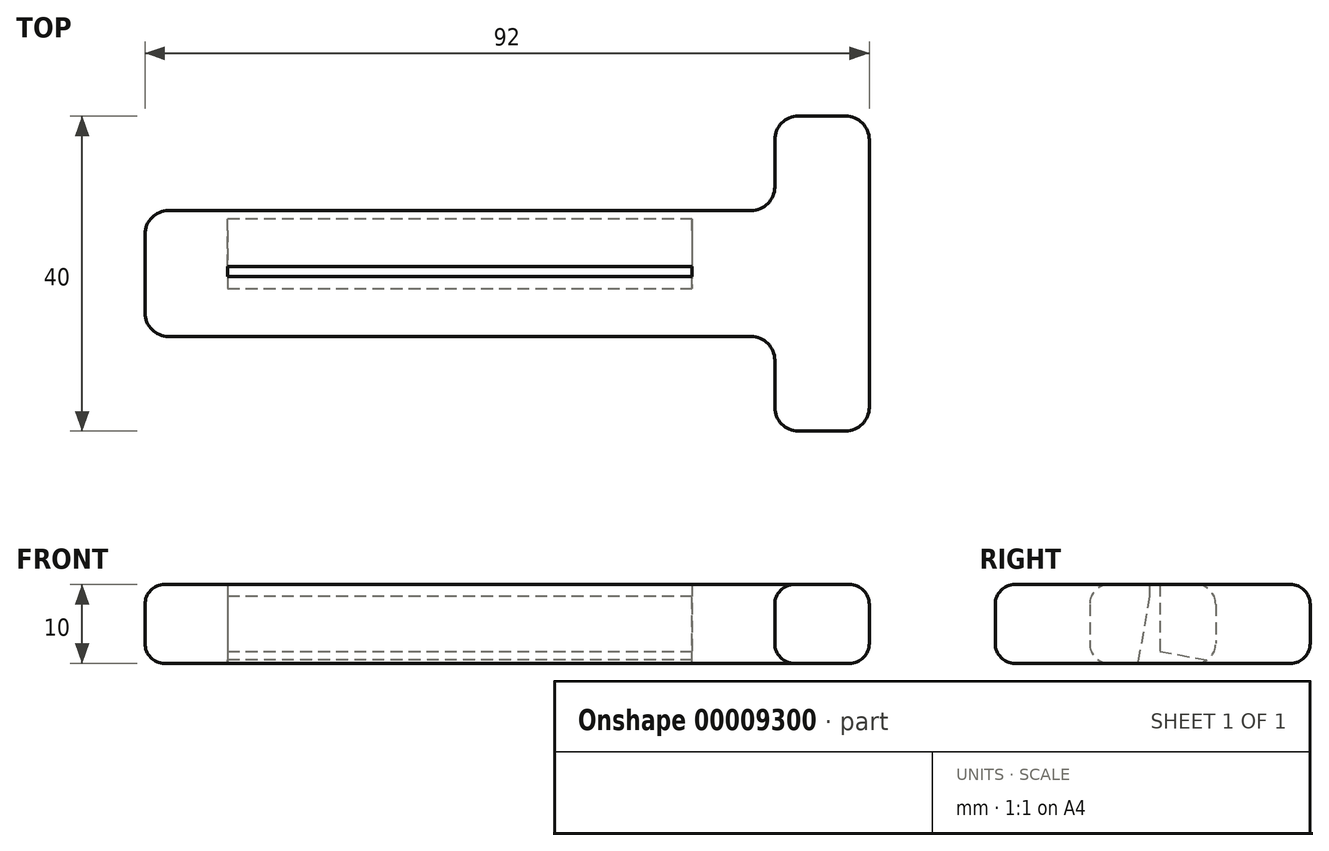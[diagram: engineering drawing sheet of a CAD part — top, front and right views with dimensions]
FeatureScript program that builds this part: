
annotation { "Feature Type Name" : "Feature", "Feature Type Description" : "" }
export const myFeature = defineFeature(function(context is Context, id is Id, definition is map)
    precondition{}
    {
        {
            var Q0;
            Q0=qCreatedBy(makeId("Top.planeOp"),FACE);
            var sketch = newSketch(context, id + "F0", { "sketchPlane" : qUnion([Q0])});
            skLineSegment(sketch, "E0.bottom", {"start": v(-31.18, 12.18) * mm, "end": v(27.82, 12.18) * mm});
            skLineSegment(sketch, "E0.top", {"start": v(-31.18, 10.88) * mm, "end": v(27.82, 10.88) * mm});
            skLineSegment(sketch, "E0.left", {"start": v(-31.18, 12.18) * mm, "end": v(-31.18, 10.88) * mm});
            skLineSegment(sketch, "E0.right", {"start": v(27.82, 12.18) * mm, "end": v(27.82, 10.88) * mm});
            skLineSegment(sketch, "E1.bottom", {"start": v(-38.68, 19.28) * mm, "end": v(35.32, 19.28) * mm});
            skLineSegment(sketch, "E1.top", {"start": v(-38.68, 3.28) * mm, "end": v(35.32, 3.28) * mm});
            skLineSegment(sketch, "E1.left", {"start": v(-41.68, 16.28) * mm, "end": v(-41.68, 6.28) * mm});
            skPoint(sketch, "E2.visualSharp", {"position": v(-41.68, 19.28) * mm});
            skArc(sketch, "E2.filletArc", {"start": v(-38.68, 19.28) * mm, "mid": v(-40.8, 18.4) * mm, "end": v(-41.68, 16.28) * mm});
            skPoint(sketch, "E3.visualSharp", {"position": v(-41.68, 3.28) * mm});
            skArc(sketch, "E3.filletArc", {"start": v(-41.68, 6.28) * mm, "mid": v(-40.8, 4.16) * mm, "end": v(-38.68, 3.28) * mm});
            skLineSegment(sketch, "E4.bottom", {"start": v(41.32, 31.28) * mm, "end": v(47.32, 31.28) * mm});
            skLineSegment(sketch, "E4.top", {"start": v(41.32, -8.72) * mm, "end": v(47.32, -8.72) * mm});
            skLineSegment(sketch, "E4.left", {"start": v(38.32, 0.28) * mm, "end": v(38.32, -5.72) * mm});
            skLineSegment(sketch, "E4.right", {"start": v(50.32, 28.28) * mm, "end": v(50.32, -5.72) * mm});
            skPoint(sketch, "E5.visualSharp", {"position": v(38.32, 31.28) * mm});
            skArc(sketch, "E5.filletArc", {"start": v(41.32, 31.28) * mm, "mid": v(39.2, 30.4) * mm, "end": v(38.32, 28.28) * mm});
            skPoint(sketch, "E6.visualSharp", {"position": v(50.32, 31.28) * mm});
            skArc(sketch, "E6.filletArc", {"start": v(50.32, 28.28) * mm, "mid": v(49.44, 30.4) * mm, "end": v(47.32, 31.28) * mm});
            skPoint(sketch, "E7.visualSharp", {"position": v(50.32, -8.72) * mm});
            skArc(sketch, "E7.filletArc", {"start": v(47.32, -8.72) * mm, "mid": v(49.44, -7.84) * mm, "end": v(50.32, -5.72) * mm});
            skPoint(sketch, "E8.visualSharp", {"position": v(38.32, -8.72) * mm});
            skArc(sketch, "E8.filletArc", {"start": v(38.32, -5.72) * mm, "mid": v(39.2, -7.84) * mm, "end": v(41.32, -8.72) * mm});
            skPoint(sketch, "E9.newPointA", {"position": v(39.32, 3.28) * mm});
            skArc(sketch, "E9.filletArc", {"start": v(38.32, 0.28) * mm, "mid": v(37.44, 2.4) * mm, "end": v(35.32, 3.28) * mm});
            skLineSegment(sketch, "E10", {"start": v(38.32, 28.28) * mm, "end": v(38.32, 22.28) * mm});
            skPoint(sketch, "E11.visualSharp", {"position": v(38.32, 19.28) * mm});
            skArc(sketch, "E11.filletArc", {"start": v(35.32, 19.28) * mm, "mid": v(37.44, 20.16) * mm, "end": v(38.32, 22.28) * mm});
            skSolve(sketch);
        }
        {
            var Q0;
            Q0=makeQuery(id+"F0.imprint","IMPRINT",FACE,{"disambiguationData":[TD([[makeQuery(id+"F0.imprint","IMPRINT",EDGE,{"derivedFrom":sQuery(id+"F0.wireOp",EDGE,"E0.bottom")}),1.0]])]});
            extrude(context, id + "F1", {"entities" : qUnion([Q0]), "depth" : 10 * mm});
        }
        {
            var Q0;
            Q0=makeQuery(id+"F1.opExtrude","CAP_EDGE",EDGE,{"disambiguationData":[OSD([sQuery(id+"F0.wireOp",EDGE,"E1.top")])],"isStart":false});
            fillet(context, id + "F2", {"entities" : qUnion([Q0]), "radius" : 2.5 * mm, "tangentPropagation" : true, "allowEdgeOverflow" : false});
        }
        {
            var Q0;
            Q0=makeQuery(id+"F1.opExtrude","CAP_EDGE",EDGE,{"disambiguationData":[OSD([sQuery(id+"F0.wireOp",EDGE,"E1.top")])],"isStart":true});
            fillet(context, id + "F3", {"entities" : qUnion([Q0]), "radius" : 2.5 * mm, "tangentPropagation" : true, "allowEdgeOverflow" : false});
        }
        {
            var Q0;
            Q0=makeQuery(id+"F1.opExtrude","CAP_EDGE",EDGE,{"disambiguationData":[OSD([sQuery(id+"F0.wireOp",EDGE,"E0.top")])],"isStart":true});
            var Q1;
            Q1=makeQuery(id+"F1.opExtrude","CAP_EDGE",EDGE,{"disambiguationData":[OSD([sQuery(id+"F0.wireOp",EDGE,"E0.bottom")])],"isStart":true});
            chamfer(context, id + "F4", {"entities" : qUnion([Q0, Q1]), "chamferType" : ChamferType.OFFSET_ANGLE, "width" : 1.5 * mm, "oppositeDirection" : false, "angle" : 80 * degree, "tangentPropagation" : true});
        }
    });
